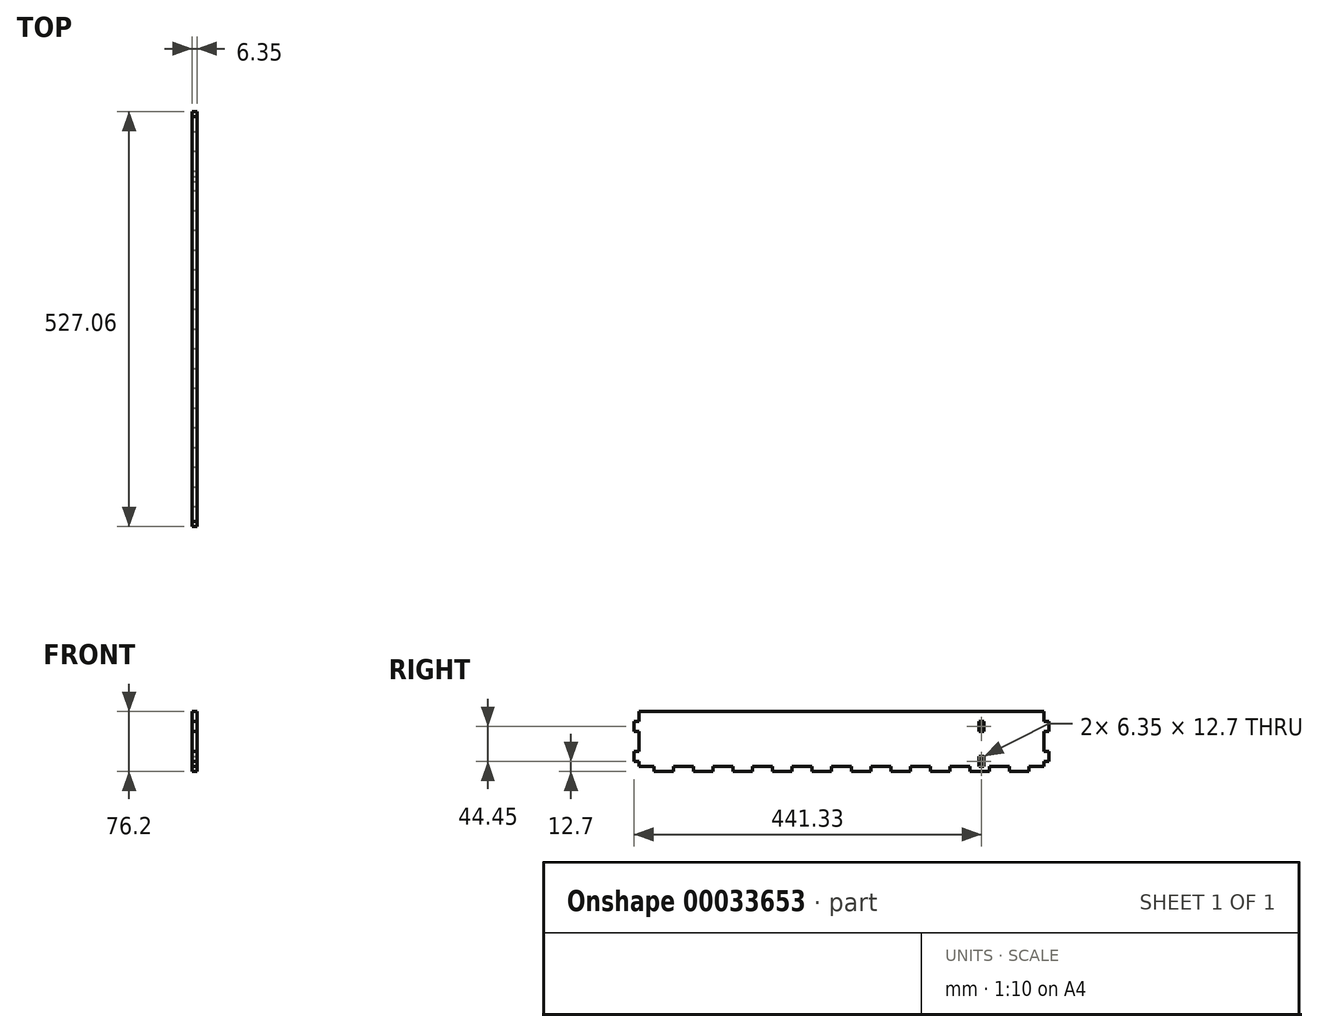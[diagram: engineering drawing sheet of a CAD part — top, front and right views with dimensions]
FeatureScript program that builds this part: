
annotation { "Feature Type Name" : "Feature", "Feature Type Description" : "" }
export const myFeature = defineFeature(function(context is Context, id is Id, definition is map)
    precondition{}
    {
        {
            var Q0;
            Q0=qCreatedBy(makeId("Right.planeOp"),FACE);
            var sketch = newSketch(context, id + "F0", { "sketchPlane" : qUnion([Q0])});
            skLineSegment(sketch, "E0.rect.bottom", {"start": v(-263.53, 38.1) * mm, "end": v(263.53, 38.1) * mm});
            skLineSegment(sketch, "E0.rect.top", {"start": v(-263.53, -38.1) * mm, "end": v(263.53, -38.1) * mm});
            skLineSegment(sketch, "E0.rect.left", {"start": v(-263.53, 38.1) * mm, "end": v(-263.53, -38.1) * mm});
            skLineSegment(sketch, "E0.rect.right", {"start": v(263.53, 38.1) * mm, "end": v(263.53, -38.1) * mm});
            skPoint(sketch, "E0.rect.middle", {"position": v(0, 0) * mm});
            skSolve(sketch);
        }
        {
            var Q0;
            Q0=makeQuery(id+"F0.imprint","IMPRINT",FACE,{"disambiguationData":[TD([[makeQuery(id+"F0.imprint","IMPRINT",EDGE,{"derivedFrom":sQuery(id+"F0.wireOp",EDGE,"E0.rect.bottom")}),-1.0]])]});
            extrude(context, id + "F1", {"entities" : qUnion([Q0]), "depth" : 6.35 * mm});
        }
        {
            var Q0;
            Q0=makeQuery(id+"F1.opExtrude","CAP_FACE",FACE,{"disambiguationData":[OSD([sQuery(id+"F0.wireOp",EDGE,"E0.rect.bottom"),sQuery(id+"F0.wireOp",EDGE,"E0.rect.top"),sQuery(id+"F0.wireOp",EDGE,"E0.rect.left"),sQuery(id+"F0.wireOp",EDGE,"E0.rect.right")])],"isStart":false});
            var sketch = newSketch(context, id + "F2", { "sketchPlane" : qUnion([Q0])});
            skLineSegment(sketch, "E1.bottom", {"start": v(-263.53, -38.1) * mm, "end": v(-238.12, -38.1) * mm});
            skLineSegment(sketch, "E1.top", {"start": v(-263.53, -31.75) * mm, "end": v(-238.12, -31.75) * mm});
            skLineSegment(sketch, "E1.left", {"start": v(-263.53, -38.1) * mm, "end": v(-263.53, -31.75) * mm});
            skLineSegment(sketch, "E1.right", {"start": v(-238.12, -38.1) * mm, "end": v(-238.12, -31.75) * mm});
            skLineSegment(sketch, "E2.1.0.0", {"start": v(-213.36, -38.1) * mm, "end": v(-187.96, -38.1) * mm});
            skLineSegment(sketch, "E2.1.0.1", {"start": v(-213.36, -31.75) * mm, "end": v(-187.96, -31.75) * mm});
            skLineSegment(sketch, "E2.1.0.2", {"start": v(-213.36, -38.1) * mm, "end": v(-213.36, -31.75) * mm});
            skLineSegment(sketch, "E2.1.0.3", {"start": v(-187.96, -38.1) * mm, "end": v(-187.96, -31.75) * mm});
            skLineSegment(sketch, "E2.2.0.0", {"start": v(-163.2, -38.1) * mm, "end": v(-137.8, -38.1) * mm});
            skLineSegment(sketch, "E2.2.0.1", {"start": v(-163.2, -31.75) * mm, "end": v(-137.8, -31.75) * mm});
            skLineSegment(sketch, "E2.2.0.2", {"start": v(-163.2, -38.1) * mm, "end": v(-163.2, -31.75) * mm});
            skLineSegment(sketch, "E2.2.0.3", {"start": v(-137.8, -38.1) * mm, "end": v(-137.8, -31.75) * mm});
            skLineSegment(sketch, "E2.3.0.0", {"start": v(-113.03, -38.1) * mm, "end": v(-87.63, -38.1) * mm});
            skLineSegment(sketch, "E2.3.0.1", {"start": v(-113.03, -31.75) * mm, "end": v(-87.63, -31.75) * mm});
            skLineSegment(sketch, "E2.3.0.2", {"start": v(-113.03, -38.1) * mm, "end": v(-113.03, -31.75) * mm});
            skLineSegment(sketch, "E2.3.0.3", {"start": v(-87.63, -38.1) * mm, "end": v(-87.63, -31.75) * mm});
            skLineSegment(sketch, "E2.4.0.0", {"start": v(-62.87, -38.1) * mm, "end": v(-37.46, -38.1) * mm});
            skLineSegment(sketch, "E2.4.0.1", {"start": v(-62.87, -31.75) * mm, "end": v(-37.46, -31.75) * mm});
            skLineSegment(sketch, "E2.4.0.2", {"start": v(-62.87, -38.1) * mm, "end": v(-62.87, -31.75) * mm});
            skLineSegment(sketch, "E2.4.0.3", {"start": v(-37.46, -38.1) * mm, "end": v(-37.46, -31.75) * mm});
            skLineSegment(sketch, "E2.5.0.0", {"start": v(-12.7, -38.1) * mm, "end": v(12.7, -38.1) * mm});
            skLineSegment(sketch, "E2.5.0.1", {"start": v(-12.7, -31.75) * mm, "end": v(12.7, -31.75) * mm});
            skLineSegment(sketch, "E2.5.0.2", {"start": v(-12.7, -38.1) * mm, "end": v(-12.7, -31.75) * mm});
            skLineSegment(sketch, "E2.5.0.3", {"start": v(12.7, -38.1) * mm, "end": v(12.7, -31.75) * mm});
            skLineSegment(sketch, "E2.6.0.0", {"start": v(37.46, -38.1) * mm, "end": v(62.86, -38.1) * mm});
            skLineSegment(sketch, "E2.6.0.1", {"start": v(37.46, -31.75) * mm, "end": v(62.86, -31.75) * mm});
            skLineSegment(sketch, "E2.6.0.2", {"start": v(37.46, -38.1) * mm, "end": v(37.46, -31.75) * mm});
            skLineSegment(sketch, "E2.6.0.3", {"start": v(62.86, -38.1) * mm, "end": v(62.86, -31.75) * mm});
            skLineSegment(sketch, "E2.7.0.0", {"start": v(87.63, -38.1) * mm, "end": v(113.03, -38.1) * mm});
            skLineSegment(sketch, "E2.7.0.1", {"start": v(87.63, -31.75) * mm, "end": v(113.03, -31.75) * mm});
            skLineSegment(sketch, "E2.7.0.2", {"start": v(87.63, -38.1) * mm, "end": v(87.63, -31.75) * mm});
            skLineSegment(sketch, "E2.7.0.3", {"start": v(113.03, -38.1) * mm, "end": v(113.03, -31.75) * mm});
            skLineSegment(sketch, "E2.8.0.0", {"start": v(137.8, -38.1) * mm, "end": v(163.2, -38.1) * mm});
            skLineSegment(sketch, "E2.8.0.1", {"start": v(137.8, -31.75) * mm, "end": v(163.2, -31.75) * mm});
            skLineSegment(sketch, "E2.8.0.2", {"start": v(137.8, -38.1) * mm, "end": v(137.8, -31.75) * mm});
            skLineSegment(sketch, "E2.8.0.3", {"start": v(163.2, -38.1) * mm, "end": v(163.2, -31.75) * mm});
            skLineSegment(sketch, "E2.9.0.0", {"start": v(187.96, -38.1) * mm, "end": v(213.36, -38.1) * mm});
            skLineSegment(sketch, "E2.9.0.1", {"start": v(187.96, -31.75) * mm, "end": v(213.36, -31.75) * mm});
            skLineSegment(sketch, "E2.9.0.2", {"start": v(187.96, -38.1) * mm, "end": v(187.96, -31.75) * mm});
            skLineSegment(sketch, "E2.9.0.3", {"start": v(213.36, -38.1) * mm, "end": v(213.36, -31.75) * mm});
            skLineSegment(sketch, "E2.direction1", {"start": v(-263.53, -38.1) * mm, "end": v(-213.36, -38.1) * mm, "construction": true});
            skLineSegment(sketch, "E3.0.10.0", {"start": v(238.13, -38.1) * mm, "end": v(263.53, -38.1) * mm});
            skLineSegment(sketch, "E3.3.10.0", {"start": v(238.13, -31.75) * mm, "end": v(263.53, -31.75) * mm});
            skLineSegment(sketch, "E3.6.10.0", {"start": v(238.13, -38.1) * mm, "end": v(238.13, -31.75) * mm});
            skLineSegment(sketch, "E3.9.10.0", {"start": v(263.53, -38.1) * mm, "end": v(263.53, -31.75) * mm});
            skLineSegment(sketch, "E4.bottom", {"start": v(-263.53, 38.1) * mm, "end": v(-257.18, 38.1) * mm});
            skLineSegment(sketch, "E4.top", {"start": v(-263.53, 25.4) * mm, "end": v(-257.18, 25.4) * mm});
            skLineSegment(sketch, "E4.left", {"start": v(-263.53, 38.1) * mm, "end": v(-263.53, 25.4) * mm});
            skLineSegment(sketch, "E4.right", {"start": v(-257.18, 38.1) * mm, "end": v(-257.18, 25.4) * mm});
            skLineSegment(sketch, "E5.bottom", {"start": v(-263.53, 12.7) * mm, "end": v(-257.18, 12.7) * mm});
            skLineSegment(sketch, "E5.top", {"start": v(-263.53, -12.7) * mm, "end": v(-257.18, -12.7) * mm});
            skLineSegment(sketch, "E5.left", {"start": v(-263.53, 12.7) * mm, "end": v(-263.53, -12.7) * mm});
            skLineSegment(sketch, "E5.right", {"start": v(-257.18, 12.7) * mm, "end": v(-257.18, -12.7) * mm});
            skLineSegment(sketch, "E6.bottom", {"start": v(-263.53, -25.4) * mm, "end": v(-257.18, -25.4) * mm});
            skLineSegment(sketch, "E6.top", {"start": v(-263.53, -31.75) * mm, "end": v(-257.18, -31.75) * mm});
            skLineSegment(sketch, "E6.left", {"start": v(-263.53, -25.4) * mm, "end": v(-263.53, -31.75) * mm});
            skLineSegment(sketch, "E6.right", {"start": v(-257.18, -25.4) * mm, "end": v(-257.18, -31.75) * mm});
            skLineSegment(sketch, "E7", {"start": v(0, 38.1) * mm, "end": v(0, -38.1) * mm, "construction": true});
            skLineSegment(sketch, "E8.bottom", {"start": v(263.53, 38.1) * mm, "end": v(257.18, 38.1) * mm});
            skLineSegment(sketch, "E8.top", {"start": v(263.53, 25.4) * mm, "end": v(257.18, 25.4) * mm});
            skLineSegment(sketch, "E8.left", {"start": v(263.53, 38.1) * mm, "end": v(263.53, 25.4) * mm});
            skLineSegment(sketch, "E8.right", {"start": v(257.18, 38.1) * mm, "end": v(257.18, 25.4) * mm});
            skLineSegment(sketch, "E9.bottom", {"start": v(263.53, 12.7) * mm, "end": v(257.18, 12.7) * mm});
            skLineSegment(sketch, "E9.top", {"start": v(263.53, -12.7) * mm, "end": v(257.18, -12.7) * mm});
            skLineSegment(sketch, "E9.left", {"start": v(263.53, 12.7) * mm, "end": v(263.53, -12.7) * mm});
            skLineSegment(sketch, "E9.right", {"start": v(257.18, 12.7) * mm, "end": v(257.18, -12.7) * mm});
            skLineSegment(sketch, "E10.bottom", {"start": v(257.18, -31.75) * mm, "end": v(263.53, -31.75) * mm});
            skLineSegment(sketch, "E10.top", {"start": v(257.18, -25.4) * mm, "end": v(263.53, -25.4) * mm});
            skLineSegment(sketch, "E10.left", {"start": v(257.18, -31.75) * mm, "end": v(257.18, -25.4) * mm});
            skLineSegment(sketch, "E10.right", {"start": v(263.53, -31.75) * mm, "end": v(263.53, -25.4) * mm});
            skSolve(sketch);
        }
        {
            var Q0;
            Q0=qSketchRegion(id+"F2",true);
            extrude(context, id + "F3", {"entities" : qUnion([Q0]), "operationType" : NewBodyOperationType.REMOVE, "endBound" : BoundingType.UP_TO_NEXT, "oppositeDirection" : true, "depth" : 25.4 * mm});
        }
        {
            var Q0;
            Q0=makeQuery(id+"F1.opExtrude","CAP_FACE",FACE,{"disambiguationData":[OSD([sQuery(id+"F0.wireOp",EDGE,"E0.rect.bottom"),sQuery(id+"F0.wireOp",EDGE,"E0.rect.top"),sQuery(id+"F0.wireOp",EDGE,"E0.rect.left"),sQuery(id+"F0.wireOp",EDGE,"E0.rect.right")])],"isStart":false});
            var sketch = newSketch(context, id + "F4", { "sketchPlane" : qUnion([Q0])});
            skLineSegment(sketch, "E11.rect.bottom", {"start": v(174.62, 12.7) * mm, "end": v(180.97, 12.7) * mm});
            skLineSegment(sketch, "E11.rect.top", {"start": v(174.62, 25.4) * mm, "end": v(180.97, 25.4) * mm});
            skLineSegment(sketch, "E11.rect.left", {"start": v(174.62, 12.7) * mm, "end": v(174.62, 25.4) * mm});
            skLineSegment(sketch, "E11.rect.right", {"start": v(180.97, 12.7) * mm, "end": v(180.97, 25.4) * mm});
            skPoint(sketch, "E11.rect.middle", {"position": v(177.8, 19.05) * mm});
            skLineSegment(sketch, "E12.rect.bottom", {"start": v(180.97, -31.75) * mm, "end": v(174.62, -31.75) * mm});
            skLineSegment(sketch, "E12.rect.top", {"start": v(180.97, -19.05) * mm, "end": v(174.62, -19.05) * mm});
            skLineSegment(sketch, "E12.rect.left", {"start": v(180.97, -31.75) * mm, "end": v(180.97, -19.05) * mm});
            skLineSegment(sketch, "E12.rect.right", {"start": v(174.62, -31.75) * mm, "end": v(174.62, -19.05) * mm});
            skPoint(sketch, "E12.rect.middle", {"position": v(177.8, -25.4) * mm});
            skSolve(sketch);
        }
        {
            var Q0;
            Q0 = qSketchRegion(id + "F4", true);
            extrude(context, id + "F5", {"entities" : qUnion([Q0]), "operationType" : NewBodyOperationType.REMOVE, "oppositeDirection" : true, "depth" : 25.4 * mm});
        }
    });
